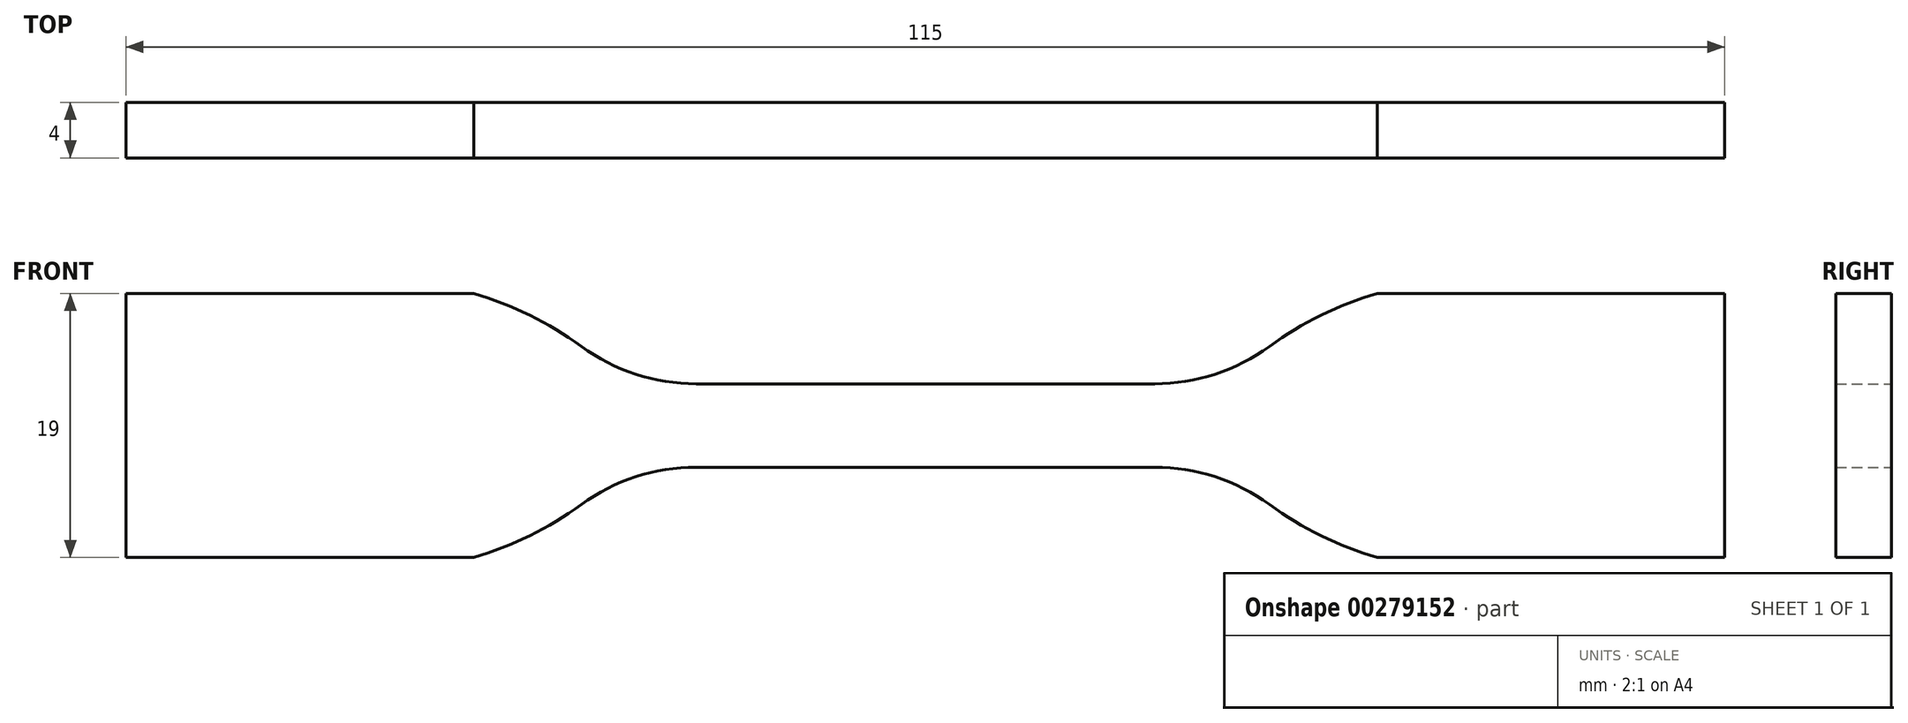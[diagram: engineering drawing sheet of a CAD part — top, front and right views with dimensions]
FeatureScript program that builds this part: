
annotation { "Feature Type Name" : "Feature", "Feature Type Description" : "" }
export const myFeature = defineFeature(function(context is Context, id is Id, definition is map)
    precondition{}
    {
        {
            var Q0;
            Q0=qCreatedBy(makeId("Front.planeOp"),FACE);
            var sketch = newSketch(context, id + "F0", { "sketchPlane" : qUnion([Q0])});
            skLineSegment(sketch, "E0", {"start": v(0, 3) * mm, "end": v(16.5, 3) * mm});
            skArc(sketch, "E1", {"start": v(16.5, 3) * mm, "mid": v(20.84, 3.69) * mm, "end": v(24.75, 5.7) * mm});
            skArc(sketch, "E2", {"start": v(24.75, 5.7) * mm, "mid": v(28.46, 7.93) * mm, "end": v(32.5, 9.5) * mm});
            skLineSegment(sketch, "E3", {"start": v(32.5, 9.5) * mm, "end": v(57.5, 9.5) * mm});
            skLineSegment(sketch, "E4", {"start": v(57.5, 9.5) * mm, "end": v(57.5, 0) * mm});
            skArc(sketch, "E5.MirrorCS", {"start": v(16.5, -3) * mm, "mid": v(20.84, -3.69) * mm, "end": v(24.75, -5.7) * mm});
            skArc(sketch, "E6.MirrorCS", {"start": v(24.75, -5.7) * mm, "mid": v(28.46, -7.93) * mm, "end": v(32.5, -9.5) * mm});
            skLineSegment(sketch, "E7.MirrorCS", {"start": v(32.5, -9.5) * mm, "end": v(57.5, -9.5) * mm});
            skLineSegment(sketch, "E8.MirrorCS", {"start": v(0, -3) * mm, "end": v(16.5, -3) * mm});
            skLineSegment(sketch, "E9.MirrorCS", {"start": v(57.5, -9.5) * mm, "end": v(57.5, 0) * mm});
            skArc(sketch, "E10.MirrorCS", {"start": v(-24.75, -5.7) * mm, "mid": v(-28.46, -7.93) * mm, "end": v(-32.5, -9.5) * mm});
            skLineSegment(sketch, "E11.MirrorCS", {"start": v(-32.5, 9.5) * mm, "end": v(-57.5, 9.5) * mm});
            skLineSegment(sketch, "E12.MirrorCS", {"start": v(-57.5, 9.5) * mm, "end": v(-57.5, 0) * mm});
            skArc(sketch, "E13.MirrorCS", {"start": v(-16.5, -3) * mm, "mid": v(-20.84, -3.69) * mm, "end": v(-24.75, -5.7) * mm});
            skArc(sketch, "E14.MirrorCS", {"start": v(-24.75, 5.7) * mm, "mid": v(-28.46, 7.93) * mm, "end": v(-32.5, 9.5) * mm});
            skArc(sketch, "E15.MirrorCS", {"start": v(-16.5, 3) * mm, "mid": v(-20.84, 3.69) * mm, "end": v(-24.75, 5.7) * mm});
            skLineSegment(sketch, "E16.MirrorCS", {"start": v(0, 3) * mm, "end": v(-16.5, 3) * mm});
            skLineSegment(sketch, "E17.MirrorCS", {"start": v(-32.5, -9.5) * mm, "end": v(-57.5, -9.5) * mm});
            skLineSegment(sketch, "E18.MirrorCS", {"start": v(0, -3) * mm, "end": v(-16.5, -3) * mm});
            skLineSegment(sketch, "E19.MirrorCS", {"start": v(-57.5, -9.5) * mm, "end": v(-57.5, 0) * mm});
            skSolve(sketch);
        }
        {
            var Q0;
            Q0=makeQuery(id+"F0.imprint","IMPRINT",FACE,{"disambiguationData":[TD([[makeQuery(id+"F0.imprint","IMPRINT",EDGE,{"derivedFrom":sQuery(id+"F0.wireOp",EDGE,"E9.MirrorCS")}),1.0]])]});
            extrude(context, id + "F1", {"entities" : qUnion([Q0]), "endBound" : BoundingType.SYMMETRIC, "depth" : 4 * mm});
        }
    });
